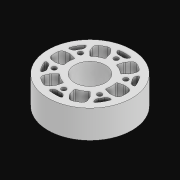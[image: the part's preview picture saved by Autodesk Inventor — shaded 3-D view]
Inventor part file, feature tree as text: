
AUTODESK INVENTOR PART (.ipt)
format: ipt  version: 2021 (Build 250183000, 183)  size: 582,144 bytes
history: native  units: in
note: dims shown in document units (in); Inventor stores cm internally (conversion verified against a paired STEP export)
features: other x10, extrude x2, sketch x2, projected_geometry x2, pattern_circular x1
ambient origin geometry x8: Origin, YZ Plane, XZ Plane, XY Plane, X Axis, Y Axis, Z Axis, Center Point
bodies: Solid1 (feature_tree)
feature tree (17):
  other  "Table"
  other  "Color = 60a Flex Wheel"
  other  "Color = 30a Flex Wheel"
  other  "Thickness = .125 in"
  other  "Thickness = 1.000 in"
  other  "Color = 40a Flex Wheel"
  other  "Thickness = .750 in"
  other  "Thickness = .250 in"
  other  "Thickness = .375 in"
  other  "Thickness = .500 in"
  extrude  "Extrusion1"  Depth=1.0in TaperAngle=0.0deg
  extrude  "Extrusion2"  [1 undecoded]
  sketch  "Sketch1"  dims[d1=0.0in d2=1.0in d3=0.0in]
  projected_geometry  "Projected Loop1"
  sketch  "Sketch2"
  projected_geometry  "Projected Loop2"
  pattern_circular  "CirPattern2"
note: 1 required parameter value undecoded (feature->parameter linkage not recoverable at this tier; creation-order binding heuristic only, values carry confidence <= 0.55)
